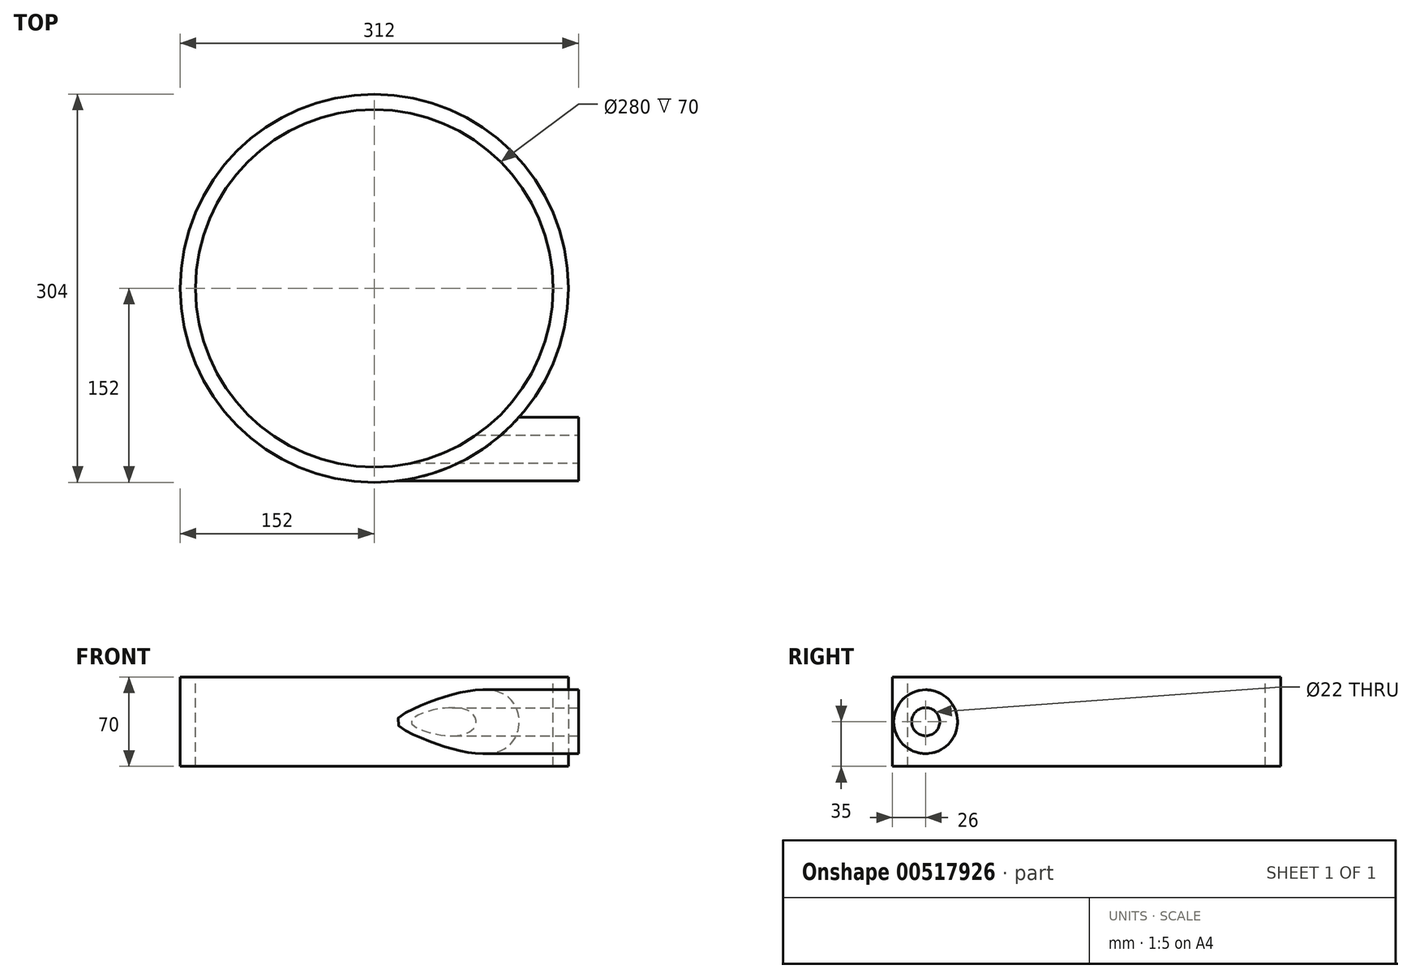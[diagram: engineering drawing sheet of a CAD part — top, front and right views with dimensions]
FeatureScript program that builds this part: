
annotation { "Feature Type Name" : "Feature", "Feature Type Description" : "" }
export const myFeature = defineFeature(function(context is Context, id is Id, definition is map)
    precondition{}
    {
        {
            var Q0;
            Q0=qCreatedBy(makeId("Top.planeOp"),FACE);
            var sketch = newSketch(context, id + "F0", { "sketchPlane" : qUnion([Q0])});
            skCircle(sketch, "E0", {"center": v(0, 0) * mm, "radius": 152 * mm});
            skSolve(sketch);
        }
        {
            var Q0;
            Q0 = qSketchRegion(id + "F0", true);
            extrude(context, id + "F1", {"entities" : qUnion([Q0]), "depth" : 70 * mm, "offsetDistance" : 25.4 * mm});
        }
        {
            var Q0;
            Q0=qCreatedBy(makeId("Right.planeOp"),FACE);
            var sketch = newSketch(context, id + "F2", { "sketchPlane" : qUnion([Q0])});
            skCircle(sketch, "E1", {"center": v(-126, 35) * mm, "radius": 25 * mm});
            skPoint(sketch, "E2", {"position": v(-126, 0) * mm});
            skSolve(sketch);
        }
        {
            var Q0;
            Q0 = qSketchRegion(id + "F2", true);
            extrude(context, id + "F3", {"entities" : qUnion([Q0]), "operationType" : NewBodyOperationType.ADD, "depth" : 160 * mm, "offsetDistance" : 25 * mm});
        }
        {
            var Q0;
            Q0=makeQuery(id+"F1.opExtrude","CAP_FACE",FACE,{"disambiguationData":[OSD([sQuery(id+"F0.wireOp",EDGE,"E0")])],"isStart":false});
            var sketch = newSketch(context, id + "F4", { "sketchPlane" : qUnion([Q0])});
            skCircle(sketch, "E3", {"center": v(0, 0) * mm, "radius": 140 * mm});
            skSolve(sketch);
        }
        {
            var Q0;
            Q0 = qSketchRegion(id + "F4", true);
            extrude(context, id + "F5", {"entities" : qUnion([Q0]), "operationType" : NewBodyOperationType.REMOVE, "oppositeDirection" : true, "depth" : 70 * mm, "offsetDistance" : 25 * mm});
        }
        {
            var Q0;
            Q0=makeQuery(id+"F3.opExtrude","CAP_FACE",FACE,{"disambiguationData":[OSD([sQuery(id+"F2.wireOp",EDGE,"E1")])],"isStart":false});
            var sketch = newSketch(context, id + "F6", { "sketchPlane" : qUnion([Q0])});
            skCircle(sketch, "E4", {"center": v(-126, 35) * mm, "radius": 11 * mm});
            skSolve(sketch);
        }
        {
            var Q0;
            Q0 = qSketchRegion(id + "F6", true);
            extrude(context, id + "F7", {"entities" : qUnion([Q0]), "operationType" : NewBodyOperationType.REMOVE, "oppositeDirection" : true, "depth" : 161.8 * mm, "offsetDistance" : 25 * mm});
        }
    });
